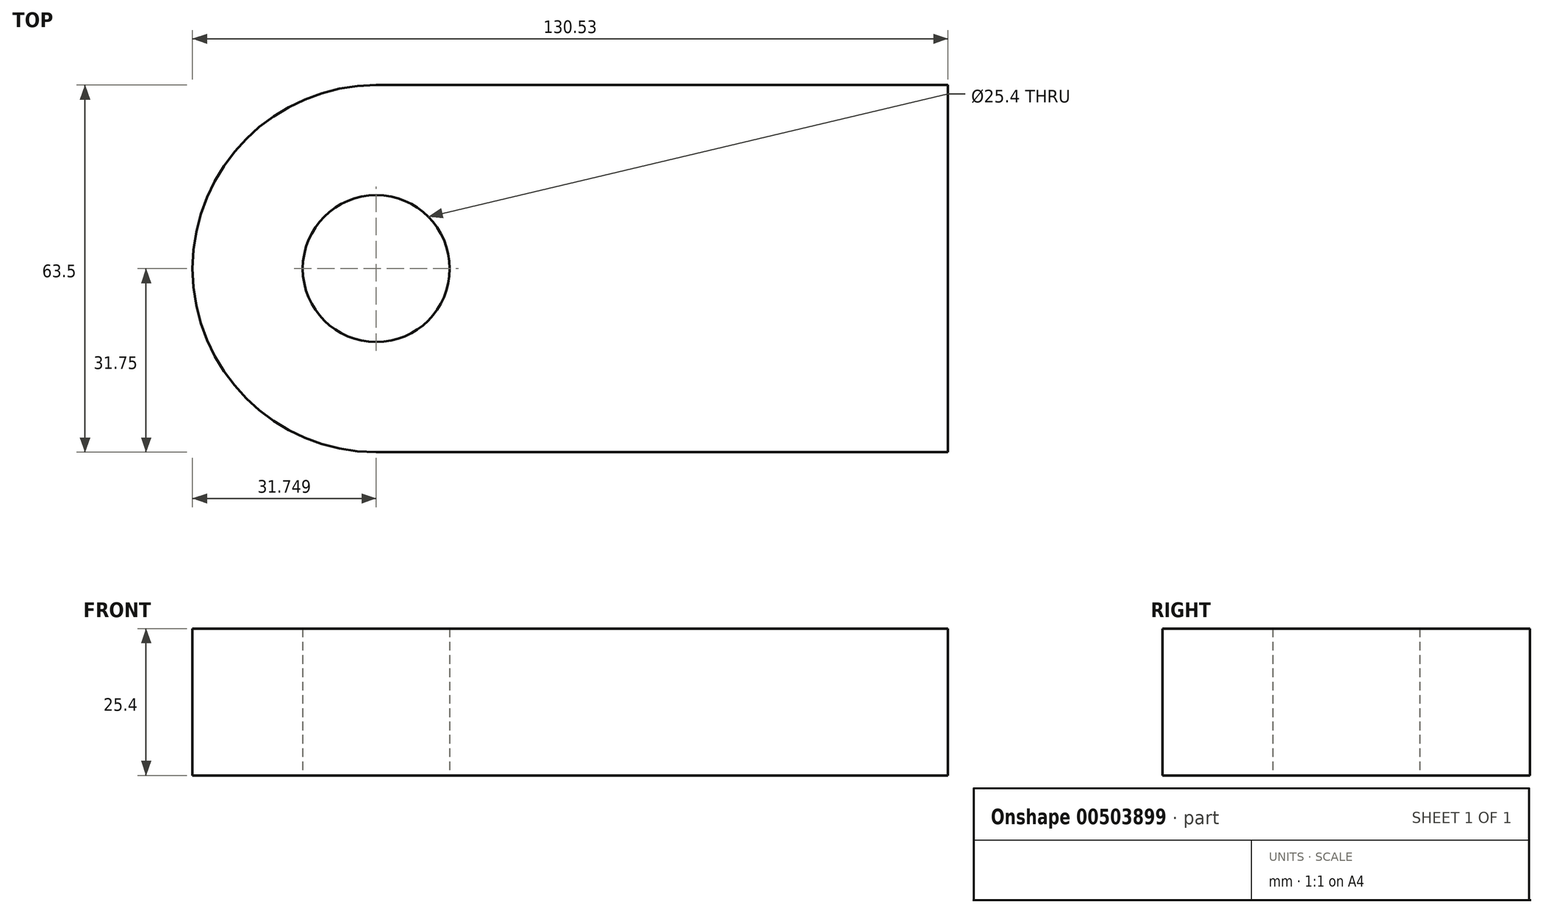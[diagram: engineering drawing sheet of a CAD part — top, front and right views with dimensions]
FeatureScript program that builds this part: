
annotation { "Feature Type Name" : "Feature", "Feature Type Description" : "" }
export const myFeature = defineFeature(function(context is Context, id is Id, definition is map)
    precondition{}
    {
        {
            var Q0;
            Q0=qCreatedBy(makeId("Top.planeOp"),FACE);
            var sketch = newSketch(context, id + "F0", { "sketchPlane" : qUnion([Q0])});
            skLineSegment(sketch, "E0.bottom", {"start": v(-48.38, 31.75) * mm, "end": v(50.4, 31.75) * mm});
            skLineSegment(sketch, "E0.top", {"start": v(-48.38, -31.75) * mm, "end": v(50.4, -31.75) * mm});
            skLineSegment(sketch, "E0.left", {"start": v(-48.38, 31.75) * mm, "end": v(-48.38, -31.75) * mm});
            skLineSegment(sketch, "E0.right", {"start": v(50.4, 31.75) * mm, "end": v(50.4, -31.75) * mm});
            skPoint(sketch, "E0.middle", {"position": v(1, 0) * mm});
            skCircle(sketch, "E1", {"center": v(-48.38, 0) * mm, "radius": 31.75 * mm});
            skCircle(sketch, "E2", {"center": v(-48.38, 0) * mm, "radius": 12.7 * mm});
            skSolve(sketch);
        }
        {
            var Q0;
            Q0 = qSketchRegion(id + "F0", true);
            extrude(context, id + "F1", {"entities" : qUnion([Q0]), "depth" : 25.4 * mm});
        }
    });
